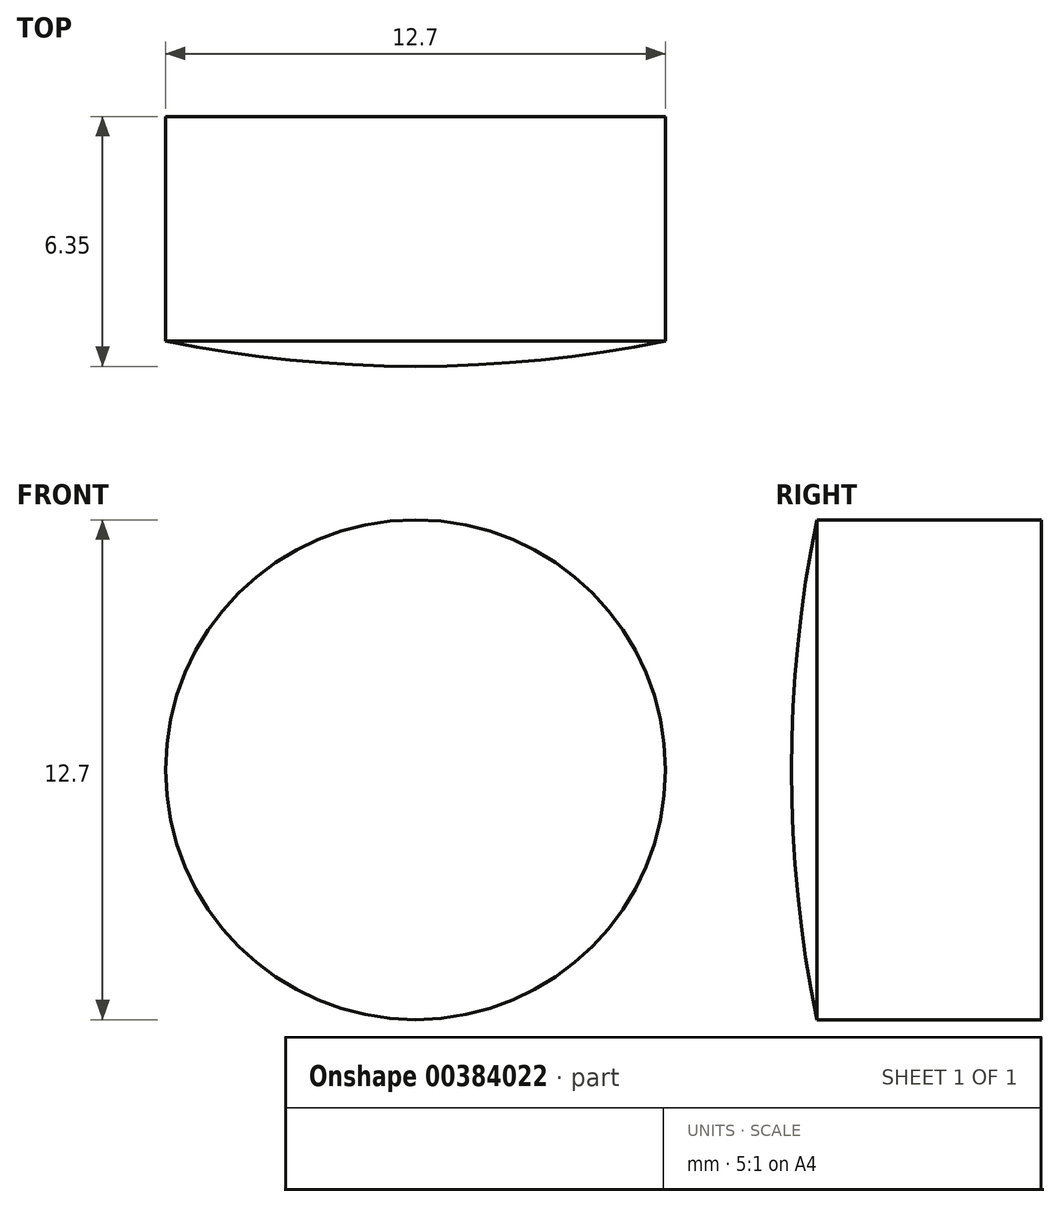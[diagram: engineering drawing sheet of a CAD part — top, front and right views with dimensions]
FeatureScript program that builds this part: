
annotation { "Feature Type Name" : "Feature", "Feature Type Description" : "" }
export const myFeature = defineFeature(function(context is Context, id is Id, definition is map)
    precondition{}
    {
        {
            var Q0;
            Q0=qCreatedBy(makeId("Front.planeOp"),FACE);
            var sketch = newSketch(context, id + "F0", { "sketchPlane" : qUnion([Q0])});
            skCircle(sketch, "E0", {"center": v(0, 0) * mm, "radius": 31.75 * mm});
            skLineSegment(sketch, "E1", {"start": v(0, 31.75) * mm, "end": v(0, -31.75) * mm});
            skSolve(sketch);
        }
        {
            var Q0;
            {var subQ0=sQuery(id+"F0.wireOp",EDGE,"E1");Q0=makeQuery(id+"F0.imprint","IMPRINT",FACE,{"disambiguationData":[TD([[makeQuery(id+"F0.imprint","IMPRINT",EDGE,{"derivedFrom":subQ0}),1.0]])]});}
            var Q1;
            Q1=sQuery(id+"F0.wireOp",EDGE,"E1");
            revolve(context, id + "F1", {"entities" : qUnion([Q0]), "axis" : qUnion([Q1]), "revolveType" : RevolveType.FULL});
        }
        {
            var Q0;
            Q0=qCreatedBy(makeId("Front.planeOp"),FACE);
            var sketch = newSketch(context, id + "F2", { "sketchPlane" : qUnion([Q0])});
            skCircle(sketch, "E2", {"center": v(0, 0) * mm, "radius": 6.35 * mm});
            skCircle(sketch, "E3", {"center": v(0, 0) * mm, "radius": 51.34 * mm});
            skSolve(sketch);
        }
        {
            var Q0;
            Q0 = qSketchRegion(id + "F2", true);
            extrude(context, id + "F3", {"entities" : qUnion([Q0]), "operationType" : NewBodyOperationType.REMOVE, "endBound" : BoundingType.THROUGH_ALL, "oppositeDirection" : true, "depth" : 25.4 * mm, "hasSecondDirection" : true, "secondDirectionBound" : SecondDirectionBoundingType.THROUGH_ALL, "secondDirectionOppositeDirection" : false, "secondDirectionDepth" : 25.4 * mm});
        }
        {
            var Q0;
            Q0=qCreatedBy(makeId("Front.planeOp"),FACE);
            var sketch = newSketch(context, id + "F4", { "sketchPlane" : qUnion([Q0])});
            skCircle(sketch, "E4", {"center": v(0, 0) * mm, "radius": 20.62 * mm});
            skSolve(sketch);
        }
        {
            var Q0;
            Q0 = qSketchRegion(id + "F4", true);
            extrude(context, id + "F5", {"entities" : qUnion([Q0]), "operationType" : NewBodyOperationType.REMOVE, "endBound" : BoundingType.THROUGH_ALL, "oppositeDirection" : true, "depth" : 25.4 * mm, "hasSecondDirection" : true, "secondDirectionOppositeDirection" : false, "secondDirectionDepth" : 25.4 * mm});
        }
    });
